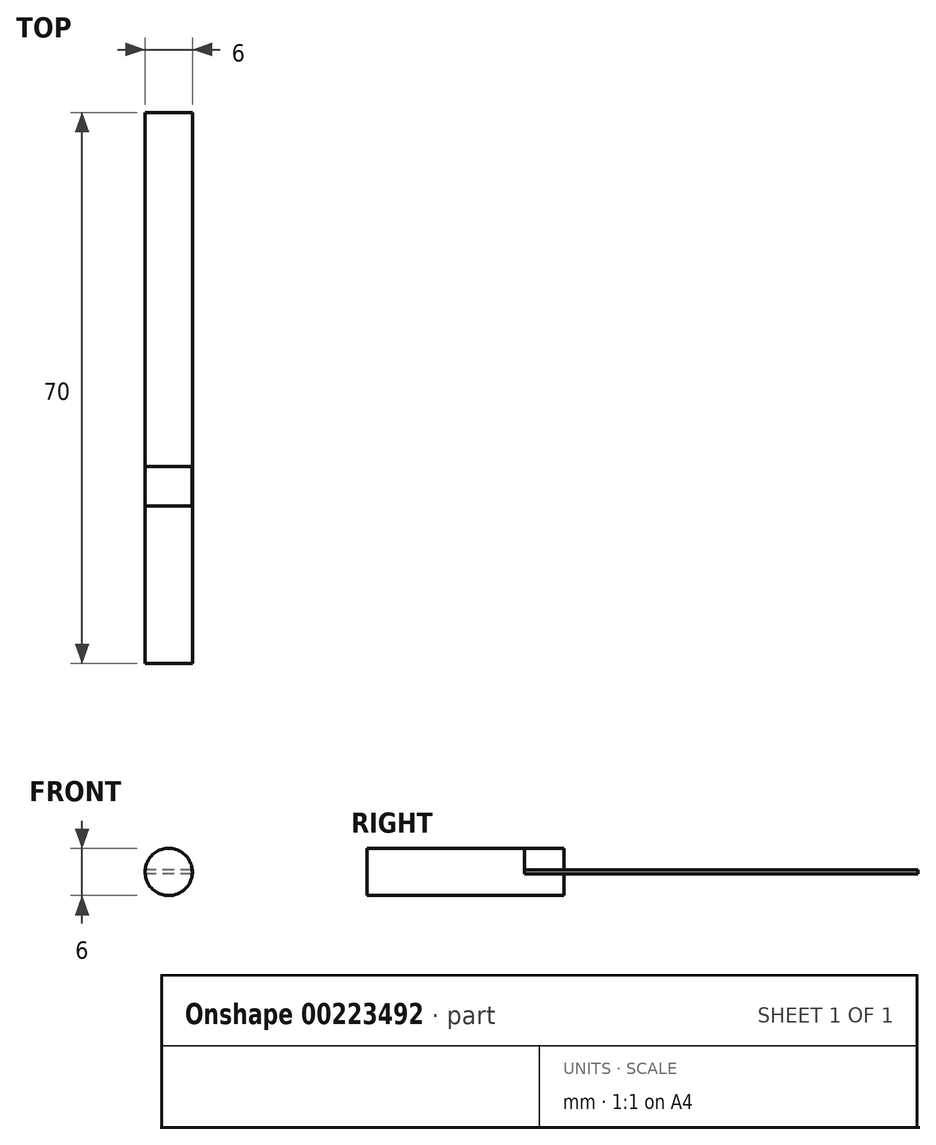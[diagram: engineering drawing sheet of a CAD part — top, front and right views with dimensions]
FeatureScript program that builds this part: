
annotation { "Feature Type Name" : "Feature", "Feature Type Description" : "" }
export const myFeature = defineFeature(function(context is Context, id is Id, definition is map)
    precondition{}
    {
        {
            var Q0;
            Q0=qCreatedBy(makeId("Front.planeOp"),FACE);
            var sketch = newSketch(context, id + "F0", { "sketchPlane" : qUnion([Q0])});
            skCircle(sketch, "E0", {"center": v(0, 0) * mm, "radius": 3 * mm});
            skSolve(sketch);
        }
        {
            var Q0;
            Q0 = qSketchRegion(id + "F0", true);
            extrude(context, id + "F1", {"entities" : qUnion([Q0]), "depth" : 25 * mm});
        }
        {
            var Q0;
            Q0=qCreatedBy(makeId("Top.planeOp"),FACE);
            var sketch = newSketch(context, id + "F2", { "sketchPlane" : qUnion([Q0])});
            skLineSegment(sketch, "E1.bottom", {"start": v(3, -5) * mm, "end": v(-3, -5) * mm});
            skLineSegment(sketch, "E1.top", {"start": v(3, 45) * mm, "end": v(-3, 45) * mm});
            skLineSegment(sketch, "E1.left", {"start": v(3, -5) * mm, "end": v(3, 45) * mm});
            skLineSegment(sketch, "E1.right", {"start": v(-3, -5) * mm, "end": v(-3, 45) * mm});
            skPoint(sketch, "E1.middle", {"position": v(0, 20) * mm});
            skSolve(sketch);
        }
        {
            var Q0;
            Q0=makeQuery(id+"F2.imprint","IMPRINT",FACE,{"disambiguationData":[TD([[makeQuery(id+"F2.imprint","IMPRINT",EDGE,{"derivedFrom":sQuery(id+"F2.wireOp",EDGE,"E1.bottom")}),-1.0]])]});
            extrude(context, id + "F3", {"entities" : qUnion([Q0]), "endBound" : BoundingType.SYMMETRIC, "depth" : .5 * mm});
        }
        {
            var Q0;
            Q0=makeQuery(id+"F3.opExtrude","SWEPT_BODY",BODY,{"disambiguationData":[OSD([sQuery(id+"F2.wireOp",EDGE,"E1.bottom"),sQuery(id+"F2.wireOp",EDGE,"E1.top"),sQuery(id+"F2.wireOp",EDGE,"E1.left"),sQuery(id+"F2.wireOp",EDGE,"E1.right")])]});
            var Q1;
            Q1=makeQuery(id+"F1.opExtrude","SWEPT_BODY",BODY,{"disambiguationData":[OSD([sQuery(id+"F0.wireOp",EDGE,"E0")])]});
            booleanBodies(context, id + "F4", {"operationType" : BooleanOperationType.SUBTRACTION, "tools" : qUnion([Q0]), "targets" : qUnion([Q1]), "keepTools" : true});
        }
        {
            var Q0;
            Q0=makeQuery(id+"F3.opExtrude","CAP_FACE",FACE,{"disambiguationData":[OSD([sQuery(id+"F2.wireOp",EDGE,"E1.bottom"),sQuery(id+"F2.wireOp",EDGE,"E1.top"),sQuery(id+"F2.wireOp",EDGE,"E1.left"),sQuery(id+"F2.wireOp",EDGE,"E1.right")])],"isStart":false});
            extrude(context, id + "F5", {"entities" : qUnion([Q0]), "depth" : 4 * mm});
        }
        {
            var Q0;
            Q0=makeQuery(id+"F5.opExtrude","SWEPT_BODY",BODY,{"disambiguationData":[OSD([sQuery(id+"F2.wireOp",EDGE,"E1.bottom"),sQuery(id+"F2.wireOp",EDGE,"E1.top"),sQuery(id+"F2.wireOp",EDGE,"E1.left"),sQuery(id+"F2.wireOp",EDGE,"E1.right")])]});
            var Q1;
            Q1=makeQuery(id+"F1.opExtrude","SWEPT_BODY",BODY,{"disambiguationData":[OSD([sQuery(id+"F0.wireOp",EDGE,"E0")])]});
            booleanBodies(context, id + "F6", {"operationType" : BooleanOperationType.INTERSECTION, "tools" : qUnion([Q0, Q1]), "keepTools" : true});
        }
        {
            var Q0;
            Q0=makeQuery(id+"F5.opExtrude","SWEPT_BODY",BODY,{"disambiguationData":[OSD([sQuery(id+"F2.wireOp",EDGE,"E1.bottom"),sQuery(id+"F2.wireOp",EDGE,"E1.top"),sQuery(id+"F2.wireOp",EDGE,"E1.left"),sQuery(id+"F2.wireOp",EDGE,"E1.right")])]});
            var Q1;
            Q1=makeQuery(id+"F1.opExtrude","SWEPT_BODY",BODY,{"disambiguationData":[OSD([sQuery(id+"F0.wireOp",EDGE,"E0")])]});
            booleanBodies(context, id + "F7", {"operationType" : BooleanOperationType.SUBTRACTION, "tools" : qUnion([Q0]), "targets" : qUnion([Q1])});
        }
    });
